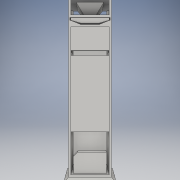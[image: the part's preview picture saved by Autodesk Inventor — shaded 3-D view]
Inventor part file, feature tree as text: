
AUTODESK INVENTOR PART (.ipt)
format: ipt  version: 2016 (Build 200138000, 138)  size: 491,008 bytes
history: native  units: in
note: dims shown in document units (in); Inventor stores cm internally (conversion verified against a paired STEP export)
features: sketch x20, extrude x18, chamfer x2, plane x1, loft x1, shell x1
ambient origin geometry x8: Origin, YZ Plane, XZ Plane, XY Plane, X Axis, Y Axis, Z Axis, Center Point
bodies: Solid1 (feature_tree)
feature tree (43):
  extrude  "Extrusion1"  Depth=18.0in
  extrude  "Extrusion3"  Depth=1.0in
  extrude  "Extrusion4"  Depth=1.0in
  extrude  "Extrusion7"  Depth=2.0in
  extrude  "Extrusion8"  Depth=16.2in
  chamfer  "Chamfer2"  Distance=13.3in
  extrude  "Extrusion9"  Depth=2.0in
  extrude  "Extrusion10"  Depth=2.0in TaperAngle=0.0deg
  sketch  "Sketch12"  dims[d13=2.0in]
  plane  "Work Plane1"
  loft  "Loft1"
  shell  "Shell1"  Thickness=17.0in
  extrude  "Extrusion12"  Depth=2.5in
  extrude  "Extrusion13"  Depth=11.75in
  extrude  "Extrusion14"  TaperAngle=0.0deg  [1 undecoded]
  extrude  "Extrusion15"  TaperAngle=0.0deg  [1 undecoded]
  extrude  "Extrusion16"  Depth=0.005in
  extrude  "Extrusion17"  Depth=0.5in TaperAngle=0.0deg
  extrude  "Extrusion18"  Depth=0.5in
  extrude  "Extrusion19"  Depth=16.0in TaperAngle=0.0deg
  extrude  "Extrusion20"  Depth=0.5in
  extrude  "Extrusion21"  Depth=18.0in
  chamfer  "Chamfer3"  Distance=16.0in
  extrude  "Extrusion22"  Depth=10.0in
  sketch  "Sketch1"  dims[d0=64.0in d1=18.0in]
  sketch  "Sketch3"  dims[d2=4.0in d3=1.0in]
  sketch  "Sketch4"  dims[d4=1.0in d5=1.0in]
  sketch  "Sketch7"  dims[d6=1.0in d7=2.0in]
  sketch  "Sketch8"  dims[d9=2.0in d10=16.2in]
  sketch  "Sketch9"  dims[d11=8.1in]
  sketch  "Sketch10"  dims[d12=2.56in]
  sketch  "Sketch13"  dims[d14=5.0in]
  sketch  "Sketch14"  dims[d15=5.0in]
  sketch  "Sketch15"  dims[d16=2.0in]
  sketch  "Sketch16"  dims[d17=18.0in]
  sketch  "Sketch17"  dims[d18=0.5in]
  sketch  "Sketch18"  dims[d19=0.5in d20=13.3in d21=0.0in]
  sketch  "Sketch19"  dims[d44=64.0in d45=18.0in d46=4.0in d47=1.0in d48=1.0in d49=1.0in d50=1.0in d51=2.0in d52=2.0in d54=16.2in d55=8.1in d56=2.56in d57=2.0in d58=5.0in d59=5.0in d60=2.0in d61=18.0in d62=0.5in d63=0.5in d64=0.85in d65=0.0in]
  sketch  "Sketch20"  dims[d66=64.0in d67=18.0in d68=4.0in d69=1.0in d70=1.0in d71=1.0in d72=1.0in d73=2.0in d74=2.0in d76=16.2in d77=8.1in d78=2.56in d79=2.0in d80=5.0in d81=5.0in d82=2.0in d83=18.0in d84=0.5in d85=0.5in d86=0.85in d87=0.0in d95=2.0in]
  sketch  "Sketch21"  dims[d96=2.0in d97=0.0in d98=2.0in d99=0.0in]
  sketch  "Sketch22"  dims[d100=2.0in d101=0.125in d102=45.0deg d103=0.5in d105=17.0in d106=0.0in]
  sketch  "Sketch23"  dims[d107=6.5in d108=0.0in d111=2.5in]
  sketch  "Sketch24"  dims[d112=6.5in d113=11.75in d114=0.0in d115=90.0deg d116=0.0in d117=90.0deg d118=0.005in d119=0.5in d120=0.0in d121=0.5in d122=16.0in d123=0.0in d124=0.5in d126=18.0in d127=16.0in d128=0.0in d129=10.0in d130=2.5in d131=8.3125in d132=0.0in d133=0.5in d134=4.0in d135=0.5in d136=1.5748in d138=360.0deg d140=2.0in d141=0.0in d144=1.5in d145=1.375in d146=0.0in d147=5.0in d148=2.0in d149=0.5in d150=13.5in d151=0.0in d152=0.5in d153=0.5in d154=0.0in d155=3.0in d156=2.0in d157=2.0in d158=21.8125in d159=0.0in d163=14.0in d164=3.0in d165=1.0in d166=9.0in d167=0.0in d168=1.75in d169=0.125in d170=45.0deg d171=10.0in d172=0.005in d173=0.0in]
note: 2 required parameter values undecoded (feature->parameter linkage not recoverable at this tier; creation-order binding heuristic only, values carry confidence <= 0.55)
